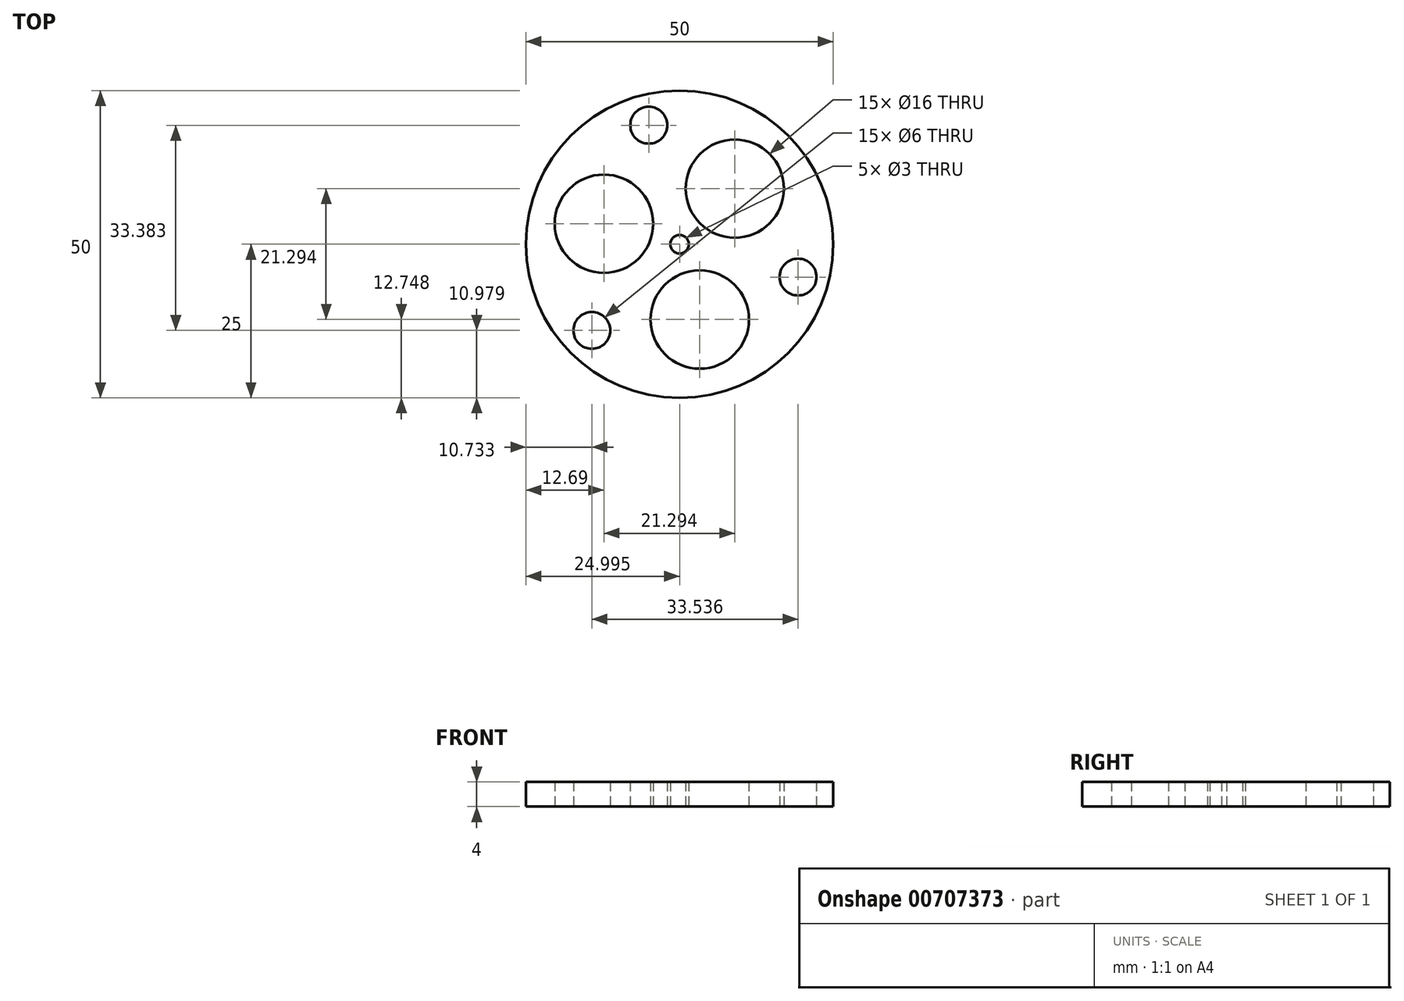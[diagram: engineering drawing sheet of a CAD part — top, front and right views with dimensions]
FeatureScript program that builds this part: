
annotation { "Feature Type Name" : "Feature", "Feature Type Description" : "" }
export const myFeature = defineFeature(function(context is Context, id is Id, definition is map)
    precondition{}
    {
        {
            var Q0;
            Q0=qCreatedBy(makeId("Top.planeOp"),FACE);
            var sketch = newSketch(context, id + "F0", { "sketchPlane" : qUnion([Q0])});
            skCircle(sketch, "E0", {"center": v(0, -0.02) * mm, "radius": 25 * mm});
            skCircle(sketch, "E1", {"center": v(9, 9.02) * mm, "radius": 8 * mm});
            skCircle(sketch, "E2.1.0", {"center": v(-12.3, 3.32) * mm, "radius": 8 * mm});
            skCircle(sketch, "E2.2.0", {"center": v(3.29, -12.27) * mm, "radius": 8 * mm});
            skPoint(sketch, "E2.center", {"position": v(0, 0.02) * mm});
            skCircle(sketch, "E3", {"center": v(0, -0.02) * mm, "radius": 12.75 * mm, "construction": true});
            skLineSegment(sketch, "E4", {"start": v(0, 0.02) * mm, "end": v(9, 9.02) * mm, "construction": true});
            skLineSegment(sketch, "E5", {"start": v(0, 0.02) * mm, "end": v(3.29, -12.27) * mm, "construction": true});
            skLineSegment(sketch, "E6", {"start": v(0, 0.02) * mm, "end": v(-12.3, 3.32) * mm, "construction": true});
            skCircle(sketch, "E7", {"center": v(0, -0.02) * mm, "radius": 20 * mm, "construction": true});
            skCircle(sketch, "E8", {"center": v(-5, 19.34) * mm, "radius": 3 * mm});
            skCircle(sketch, "E9.1.0", {"center": v(-14.26, -14.04) * mm, "radius": 3 * mm});
            skCircle(sketch, "E9.2.0", {"center": v(19.28, -5.36) * mm, "radius": 3 * mm});
            skCircle(sketch, "E10", {"center": v(0, -0.02) * mm, "radius": 1.5 * mm});
            skSolve(sketch);
        }
        {
            var Q0;
            Q0=makeQuery(id+"F0.imprint","IMPRINT",FACE,{"disambiguationData":[TD([[makeQuery(id+"F0.imprint","IMPRINT",EDGE,{"derivedFrom":sQuery(id+"F0.wireOp",EDGE,"E0")}),1.0]])]});
            extrude(context, id + "F1", {"entities" : qUnion([Q0]), "depth" : 4 * mm, "offsetDistance" : 25 * mm});
        }
    });
